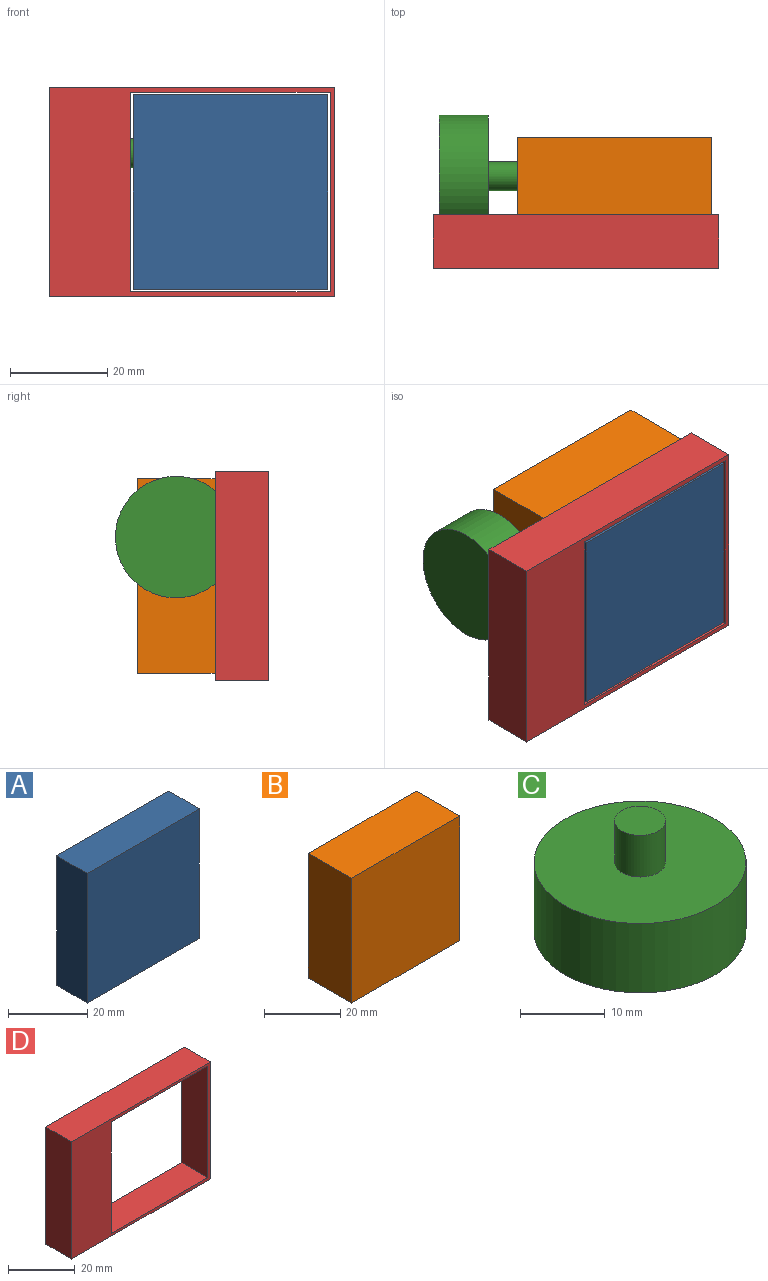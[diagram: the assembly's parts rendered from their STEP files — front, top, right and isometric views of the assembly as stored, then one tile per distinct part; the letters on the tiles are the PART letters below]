
ASSEMBLY  parts=4 mates=3
PART A: 6 faces, bbox 40x11x40 mm
  f0: plane 40x11mm, normal (0,0,1), area 440mm2, adj f1,f3,f4,f5
  f1: plane 40x11mm, normal (-1,0,0), area 440mm2, adj f0,f2,f4,f5
  f2: plane 40x11mm, normal (0,0,-1), area 440mm2, adj f1,f3,f4,f5
  f3: plane 40x11mm, normal (1,0,0), area 440mm2, adj f0,f2,f4,f5
  f4: plane 40x40mm, normal (0,-1,0), area 1600mm2, adj f0,f1,f2,f3
  f5: plane 40x40mm, normal (0,1,0), area 1600mm2, adj f0,f1,f2,f3
PART B: 6 faces, bbox 40x16x40 mm
  f0: plane 40x16mm, normal (0,0,1), area 640mm2, adj f1,f3,f4,f5
  f1: plane 40x16mm, normal (-1,0,0), area 640mm2, adj f0,f2,f4,f5
  f2: plane 40x16mm, normal (0,0,-1), area 640mm2, adj f1,f3,f4,f5
  f3: plane 40x16mm, normal (1,0,0), area 640mm2, adj f0,f2,f4,f5
  f4: plane 40x40mm, normal (0,-1,0), area 1600mm2, adj f0,f1,f2,f3
  f5: plane 40x40mm, normal (0,1,0), area 1600mm2, adj f0,f1,f2,f3
PART C: 5 faces, bbox 25x25x16 mm
  f0: cylinder r=12.5mm len=25mm, axis (0,0,-1), area 785.4mm2, adj f1,f2
  f1: plane 25x25mm, normal (0,0,1), area 462.6mm2, adj f0,f3
  f2: plane 25x25mm, normal (0,0,-1), area 490.9mm2, adj f0
  f3: cylinder r=3mm len=6mm, axis (0,0,-1), area 113.1mm2, adj f1,f4
  f4: plane 6x6mm, normal (0,0,1), area 28.3mm2, adj f3
PART D: 17 faces, bbox 58.8x11x43 mm
  f0: plane 22.98x1mm, normal (-1,0,0), area 22.2mm2, adj f10,f11,f12,f14
  f1: plane 41x1mm, normal (1,0,0), area 41mm2, adj f5,f7,f10,f12
  f2: plane 41x1mm, normal (1,0,0), area 41mm2, adj f5,f7,f9,f13
  f3: plane 43x11mm, normal (1,0,0), area 473mm2, adj f4,f8,f9,f10
  f4: plane 58.8x11mm, normal (0,0,1), area 646.8mm2, adj f3,f9,f10,f16
  f5: plane 57x11mm, normal (0,0,-1), area 595mm2, adj f1,f2,f6,f9,f10,f12,f13,f15
  f6: plane 41x11mm, normal (-1,0,0), area 451mm2, adj f5,f7,f9,f10
  f7: plane 57x11mm, normal (0,0,1), area 595mm2, adj f1,f2,f6,f9,f10,f12,f13,f15
  f8: plane 58.8x11mm, normal (0,0,-1), area 646.8mm2, adj f3,f9,f10,f16
  f9: plane 58.8x43mm, normal (0,-1,0), area 847.4mm2, adj f2,f3,f4,f5,f6,f7,f8,f16
  f10: plane 58.8x43mm, normal (0,1,0), area 502.7mm2, adj f0,f1,f3,f4,f5,f6,f7,f8
  f11: cylinder r=14mm len=15mm, axis (1,0,0), area 18.9mm2, adj f0,f10,f12,f15
  f12: plane 41x16mm, normal (0,-1,0), area 334.3mm2, adj f0,f1,f5,f7,f11,f14,f15
  f13: plane 41x16mm, normal (0,1,0), area 656mm2, adj f2,f5,f7,f15
  f14: cylinder r=14mm len=15mm, axis (1,0,0), area 18.9mm2, adj f0,f10,f12,f15
  f15: plane 41x10mm, normal (1,0,0), area 391.2mm2, adj f5,f7,f10,f11,f12,f13,f14
  f16: plane 43x11mm, normal (-1,0,0), area 473mm2, adj f4,f8,f9,f10
PLACE A t=(-20.59,4.59,3.01)mm
PLACE B t=(-20.59,20.59,3.01)mm
PLACE C rot(axis=(-0.58,0.58,-0.58),120deg) t=(-56.59,12.59,11.01)mm
PLACE D t=(-20.59,4.59,3.01)mm
MATE planar A.f4 <-> D.f9  axis (0,-1,0) through (-20.59,-6.41,3.01)mm
MATE planar A.f5 <-> B.f4  axis (0,1,0) through (-20.59,4.59,3.01)mm
MATE planar C.f3 <-> B.f1  axis (-1,0,0) through (-40.59,12.59,11.01)mm
